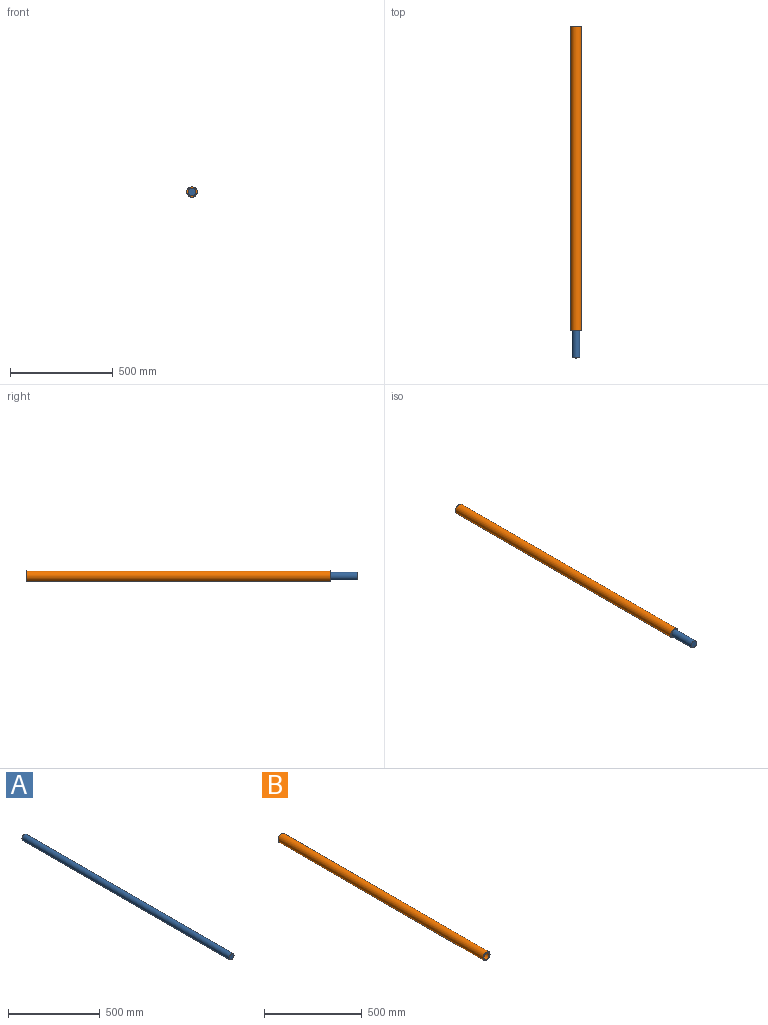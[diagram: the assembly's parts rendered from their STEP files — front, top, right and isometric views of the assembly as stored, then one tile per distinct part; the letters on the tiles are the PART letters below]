
ASSEMBLY  parts=2 mates=1
PART A: 3 faces, bbox 38.1x1600.2x38.1 mm
  f0: cylinder r=19.05mm len=1600.2mm, axis (0,1,0), area 191535.4mm2, adj f1,f2
  f1: plane 38.1x38.1mm, normal (0,-1,0), area 1140.1mm2, adj f0
  f2: plane 38.1x38.1mm, normal (0,1,0), area 1140.1mm2, adj f0
PART B: 5 faces, bbox 50.8x1482.7x50.8 mm
  f0: cylinder r=25.4mm len=1482.73mm, axis (0,1,0), area 236632.4mm2, adj f1,f3
  f1: plane 50.8x50.8mm, normal (0,1,0), area 2026.8mm2, adj f0
  f2: cylinder r=19.05mm len=1473.2mm, axis (0,1,0), area 176334.2mm2, adj f3,f4
  f3: plane 50.8x50.8mm, normal (0,-1,0), area 886.7mm2, adj f0,f2
  f4: plane 38.1x38.1mm, normal (0,-1,0), area 1140.1mm2, adj f2
PLACE A rot(axis=(1,0,0),180deg) t=(-154.73,-1464.53,-86.14)mm
PLACE B t=(-154.73,153.13,-86.14)mm fixed
MATE slider A.f0 <-> B.f0  axis (0,-1,0) through (-154.73,-664.43,-86.14)mm
